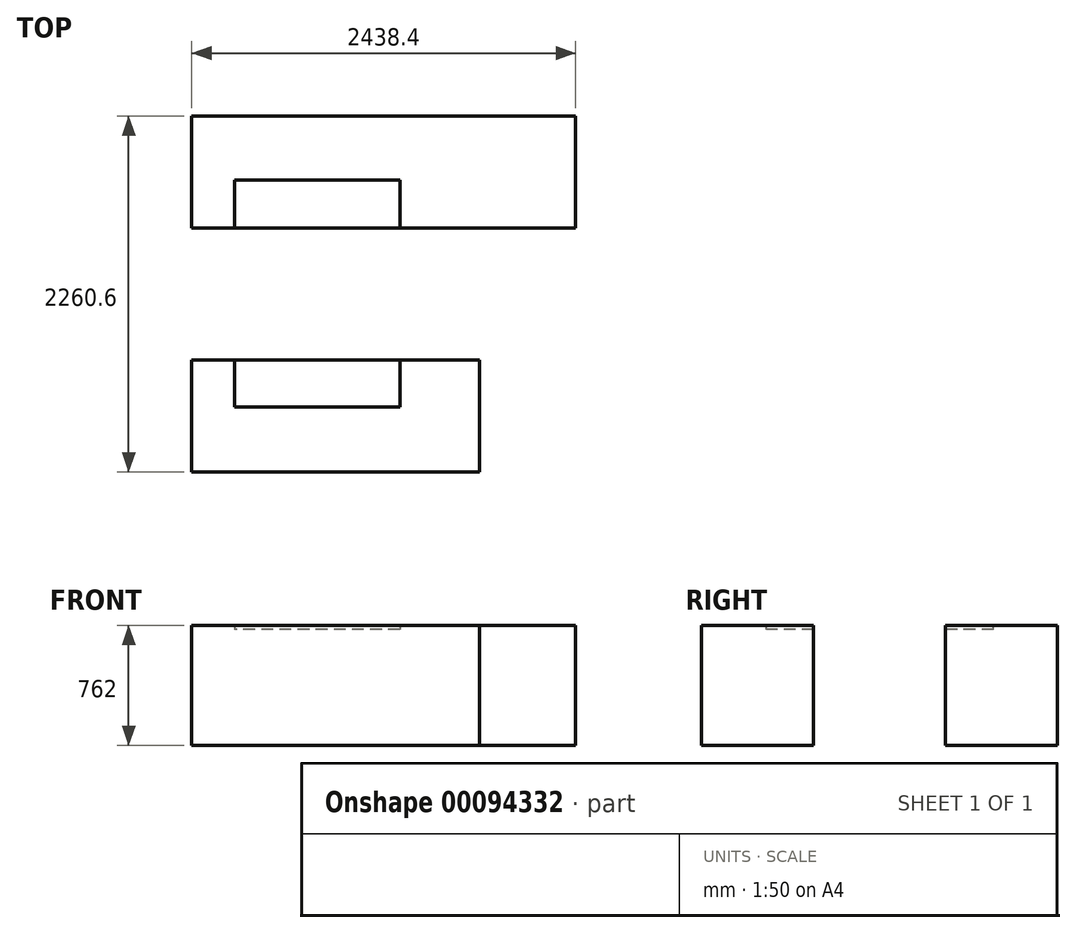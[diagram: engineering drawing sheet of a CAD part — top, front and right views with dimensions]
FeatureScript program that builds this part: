
annotation { "Feature Type Name" : "Feature", "Feature Type Description" : "" }
export const myFeature = defineFeature(function(context is Context, id is Id, definition is map)
    precondition{}
    {
        {
            var Q0;
            Q0=qCreatedBy(makeId("Top.planeOp"),FACE);
            var sketch = newSketch(context, id + "F0", { "sketchPlane" : qUnion([Q0])});
            skLineSegment(sketch, "E0.bottom", {"start": v(0, 0) * mm, "end": v(-2438.4, 0) * mm});
            skLineSegment(sketch, "E0.top", {"start": v(0, -711.2) * mm, "end": v(-2438.4, -711.2) * mm});
            skLineSegment(sketch, "E0.left", {"start": v(0, 0) * mm, "end": v(0, -711.2) * mm});
            skLineSegment(sketch, "E0.right", {"start": v(-2438.4, 0) * mm, "end": v(-2438.4, -711.2) * mm});
            skLineSegment(sketch, "E1.bottom", {"start": v(-609.6, -1549.4) * mm, "end": v(-2438.4, -1549.4) * mm});
            skLineSegment(sketch, "E1.top", {"start": v(-609.6, -2260.6) * mm, "end": v(-2438.4, -2260.6) * mm});
            skLineSegment(sketch, "E1.left", {"start": v(-609.6, -1549.4) * mm, "end": v(-609.6, -2260.6) * mm});
            skLineSegment(sketch, "E1.right", {"start": v(-2438.4, -1549.4) * mm, "end": v(-2438.4, -2260.6) * mm});
            skSolve(sketch);
        }
        {
            var Q0;
            Q0 = qSketchRegion(id + "F0", true);
            extrude(context, id + "F1", {"entities" : qUnion([Q0]), "depth" : 762 * mm});
        }
        {
            var Q0;
            Q0=makeQuery(id+"F1.opExtrude","CAP_FACE",FACE,{"disambiguationData":[OSD([sQuery(id+"F0.wireOp",EDGE,"E0.bottom"),sQuery(id+"F0.wireOp",EDGE,"E0.top"),sQuery(id+"F0.wireOp",EDGE,"E0.left"),sQuery(id+"F0.wireOp",EDGE,"E0.right")])],"isStart":false});
            var sketch = newSketch(context, id + "F2", { "sketchPlane" : qUnion([Q0])});
            skLineSegment(sketch, "E2.bottom", {"start": v(-2167.63, -407.28) * mm, "end": v(-1116.47, -407.28) * mm});
            skLineSegment(sketch, "E2.top", {"start": v(-2167.63, -1849.34) * mm, "end": v(-1116.47, -1849.34) * mm});
            skLineSegment(sketch, "E2.left", {"start": v(-2167.63, -407.28) * mm, "end": v(-2167.63, -1849.34) * mm});
            skLineSegment(sketch, "E2.right", {"start": v(-1116.47, -407.28) * mm, "end": v(-1116.47, -1849.34) * mm});
            skSolve(sketch);
        }
        {
            var Q0;
            Q0 = qSketchRegion(id + "F2", true);
            extrude(context, id + "F3", {"entities" : qUnion([Q0]), "operationType" : NewBodyOperationType.REMOVE, "oppositeDirection" : true, "depth" : 25.4 * mm});
        }
    });
